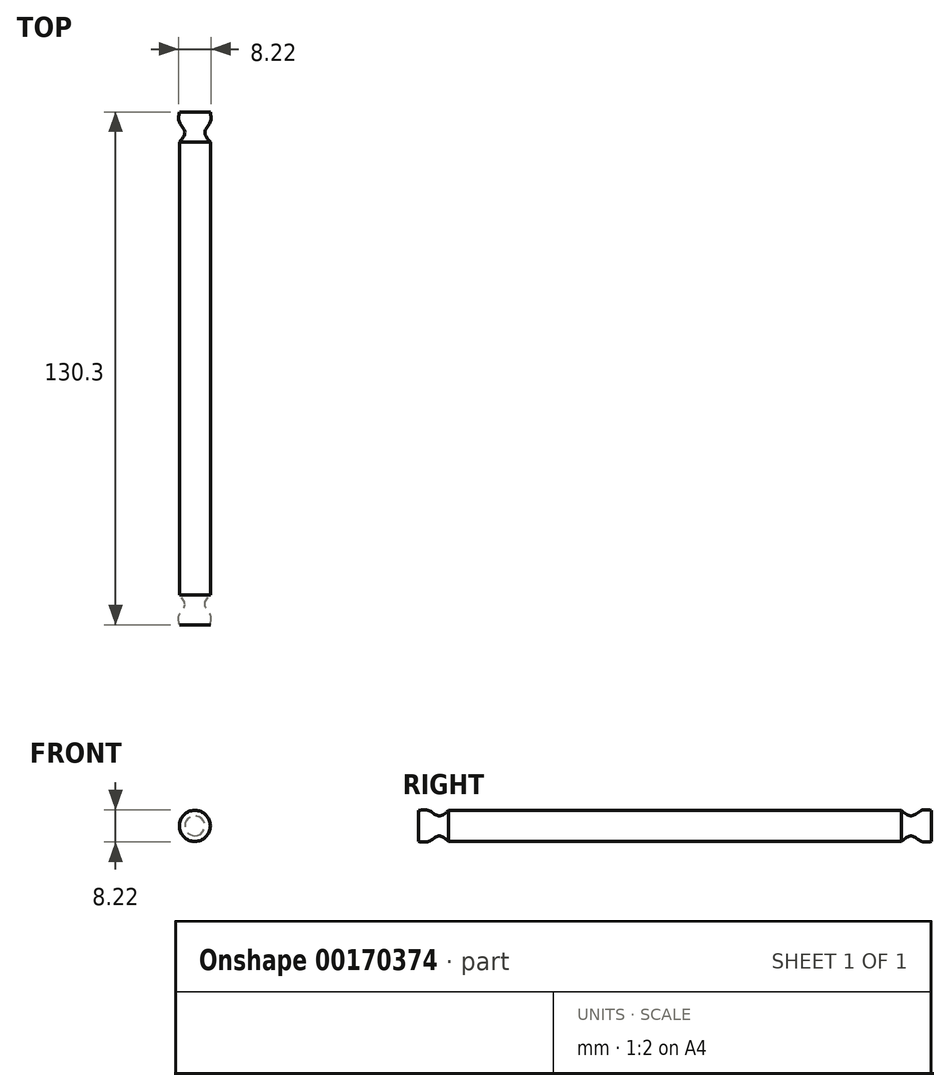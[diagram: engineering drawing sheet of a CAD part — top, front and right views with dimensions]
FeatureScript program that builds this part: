
annotation { "Feature Type Name" : "Feature", "Feature Type Description" : "" }
export const myFeature = defineFeature(function(context is Context, id is Id, definition is map)
    precondition{}
    {
        {
            var Q0;
            Q0=qCreatedBy(makeId("Front.planeOp"),FACE);
            var sketch = newSketch(context, id + "F0", { "sketchPlane" : qUnion([Q0])});
            skPoint(sketch, "E0.middle", {"position": v(0, 0) * mm});
            skCircle(sketch, "E1", {"center": v(0, 0) * mm, "radius": 3.94 * mm});
            skSolve(sketch);
        }
        {
            var Q0;
            Q0=qCreatedBy(makeId("Front.planeOp"),FACE);
            cPlane(context, id + "F1", {"entities" : qUnion([Q0]), "cplaneType" : CPlaneType.OFFSET, "offset" : 2.54 * mm, "width" : 152.4 * mm, "height" : 152.4 * mm});
        }
        {
            var Q0;
            Q0=qCreatedBy(id+"F1.planeOp",FACE);
            var sketch = newSketch(context, id + "F2", { "sketchPlane" : qUnion([Q0])});
            skCircle(sketch, "E2", {"center": v(0, 0) * mm, "radius": 3.94 * mm});
            skSolve(sketch);
        }
        {
            var Q0;
            Q0=qCreatedBy(id+"F1.planeOp",FACE);
            cPlane(context, id + "F3", {"entities" : qUnion([Q0]), "cplaneType" : CPlaneType.OFFSET, "offset" : 2.54 * mm, "width" : 152.4 * mm, "height" : 152.4 * mm});
        }
        {
            var Q0;
            Q0=qCreatedBy(id+"F3.planeOp",FACE);
            var sketch = newSketch(context, id + "F4", { "sketchPlane" : qUnion([Q0])});
            skCircle(sketch, "E3", {"center": v(0, 0) * mm, "radius": 2.54 * mm});
            skSolve(sketch);
        }
        {
            var Q0;
            Q0=qCreatedBy(makeId("Front.planeOp"),FACE);
            cPlane(context, id + "F5", {"entities" : qUnion([Q0]), "cplaneType" : CPlaneType.OFFSET, "offset" : 7.62 * mm, "width" : 152.4 * mm, "height" : 152.4 * mm});
        }
        {
            var Q0;
            Q0=qCreatedBy(id+"F5.planeOp",FACE);
            var sketch = newSketch(context, id + "F6", { "sketchPlane" : qUnion([Q0])});
            skCircle(sketch, "E4", {"center": v(0, 0) * mm, "radius": 3.94 * mm});
            skSolve(sketch);
        }
        {
            var Q0;
            Q0=qCreatedBy(makeId("Front.planeOp"),FACE);
            cPlane(context, id + "F7", {"entities" : qUnion([Q0]), "cplaneType" : CPlaneType.OFFSET, "offset" : 122.68 * mm, "width" : 152.4 * mm, "height" : 152.4 * mm});
        }
        {
            var Q0;
            Q0=qCreatedBy(id+"F7.planeOp",FACE);
            var sketch = newSketch(context, id + "F8", { "sketchPlane" : qUnion([Q0])});
            skCircle(sketch, "E5", {"center": v(0, 0) * mm, "radius": 3.94 * mm});
            skSolve(sketch);
        }
        {
            var Q0;
            Q0=qCreatedBy(makeId("Front.planeOp"),FACE);
            cPlane(context, id + "F9", {"entities" : qUnion([Q0]), "cplaneType" : CPlaneType.OFFSET, "offset" : 125.22 * mm, "width" : 152.4 * mm, "height" : 152.4 * mm});
        }
        {
            var Q0;
            Q0=qCreatedBy(id+"F9.planeOp",FACE);
            var sketch = newSketch(context, id + "F10", { "sketchPlane" : qUnion([Q0])});
            skCircle(sketch, "E6", {"center": v(0, 0) * mm, "radius": 2.54 * mm});
            skSolve(sketch);
        }
        {
            var Q0;
            Q0=qCreatedBy(makeId("Front.planeOp"),FACE);
            cPlane(context, id + "F11", {"entities" : qUnion([Q0]), "cplaneType" : CPlaneType.OFFSET, "offset" : 127.76 * mm, "width" : 152.4 * mm, "height" : 152.4 * mm});
        }
        {
            var Q0;
            Q0=qCreatedBy(id+"F11.planeOp",FACE);
            var sketch = newSketch(context, id + "F12", { "sketchPlane" : qUnion([Q0])});
            skCircle(sketch, "E7", {"center": v(0, 0) * mm, "radius": 3.94 * mm});
            skSolve(sketch);
        }
        {
            var Q0;
            Q0=qCreatedBy(makeId("Front.planeOp"),FACE);
            cPlane(context, id + "F13", {"entities" : qUnion([Q0]), "cplaneType" : CPlaneType.OFFSET, "offset" : 130.3 * mm, "width" : 152.4 * mm, "height" : 152.4 * mm});
        }
        {
            var Q0;
            Q0=qCreatedBy(id+"F13.planeOp",FACE);
            var sketch = newSketch(context, id + "F14", { "sketchPlane" : qUnion([Q0])});
            skCircle(sketch, "E8", {"center": v(0, 0) * mm, "radius": 3.94 * mm});
            skSolve(sketch);
        }
        {
            var Q0;
            Q0 = qSketchRegion(id + "F0", true);
            var Q1;
            Q1 = qSketchRegion(id + "F2", true);
            var Q2;
            Q2 = qSketchRegion(id + "F4", true);
            var Q3;
            Q3 = qSketchRegion(id + "F6", true);
            loft(context, id + "F15", {"sheetProfilesArray" : [{ "sheetProfileEntities" : qUnion([Q0]) }, { "sheetProfileEntities" : qUnion([Q1]) }, { "sheetProfileEntities" : qUnion([Q2]) }, { "sheetProfileEntities" : qUnion([Q3]) }]});
        }
        {
            var Q0;
            Q0 = qSketchRegion(id + "F8", true);
            var Q1;
            Q1 = qSketchRegion(id + "F10", true);
            var Q2;
            Q2 = qSketchRegion(id + "F12", true);
            var Q3;
            Q3 = qSketchRegion(id + "F14", true);
            loft(context, id + "F16", {"sheetProfilesArray" : [{ "sheetProfileEntities" : qUnion([Q0]) }, { "sheetProfileEntities" : qUnion([Q1]) }, { "sheetProfileEntities" : qUnion([Q2]) }, { "sheetProfileEntities" : qUnion([Q3]) }]});
        }
        {
            var Q0;
            Q0 = qSketchRegion(id + "F6", true);
            extrude(context, id + "F17", {"entities" : qUnion([Q0]), "depth" : 115.06 * mm});
        }
    });
